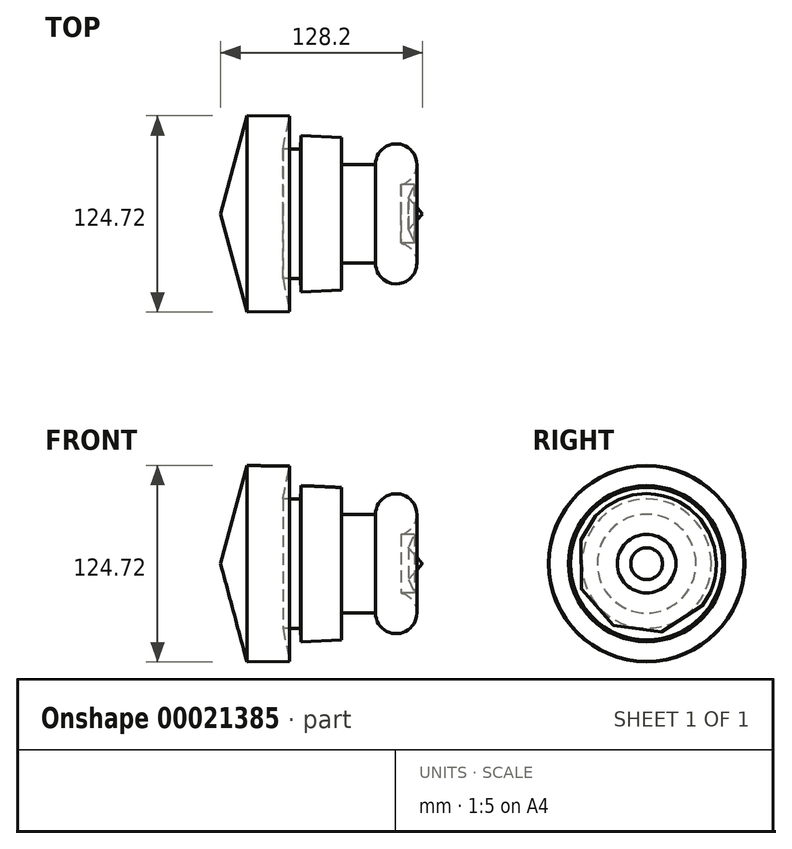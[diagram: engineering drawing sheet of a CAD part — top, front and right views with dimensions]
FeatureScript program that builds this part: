
annotation { "Feature Type Name" : "Feature", "Feature Type Description" : "" }
export const myFeature = defineFeature(function(context is Context, id is Id, definition is map)
    precondition{}
    {
        {
            var Q0;
            Q0=qCreatedBy(makeId("Front.planeOp"),FACE);
            var sketch = newSketch(context, id + "F0", { "sketchPlane" : qUnion([Q0])});
            skLineSegment(sketch, "E0", {"start": v(-63.13, 0) * mm, "end": v(65.07, 0) * mm});
            skLineSegment(sketch, "E1", {"start": v(65.07, 0) * mm, "end": v(56.16, 10.07) * mm});
            skLineSegment(sketch, "E2", {"start": v(56.16, 10.07) * mm, "end": v(60.03, 18.6) * mm});
            skLineSegment(sketch, "E3", {"start": v(60.03, 18.6) * mm, "end": v(45.32, 18.6) * mm});
            skArc(sketch, "E4", {"start": v(45.32, 18.6) * mm, "mid": v(58.65, 39.45) * mm, "end": v(35.25, 31.37) * mm});
            skLineSegment(sketch, "E5", {"start": v(35.25, 31.37) * mm, "end": v(13.56, 31.34) * mm});
            skLineSegment(sketch, "E6", {"start": v(13.56, 31.34) * mm, "end": v(13.53, 48.41) * mm});
            skLineSegment(sketch, "E7", {"start": v(13.53, 48.41) * mm, "end": v(-12, 49.58) * mm});
            skLineSegment(sketch, "E8", {"start": v(-12, 49.58) * mm, "end": v(-12.4, 41.05) * mm});
            skLineSegment(sketch, "E9", {"start": v(-12.4, 41.05) * mm, "end": v(-23.63, 41.05) * mm});
            skLineSegment(sketch, "E10", {"start": v(-23.63, 41.05) * mm, "end": v(-19.37, 61.97) * mm});
            skLineSegment(sketch, "E11", {"start": v(-19.37, 61.97) * mm, "end": v(-46.48, 62.36) * mm});
            skLineSegment(sketch, "E12", {"start": v(-46.48, 62.36) * mm, "end": v(-63.13, 0) * mm});
            skSolve(sketch);
        }
        {
            var Q0;
            Q0 = qSketchRegion(id + "F0", true);
            var Q1;
            Q1=sQuery(id+"F0.wireOp",EDGE,"E0");
            revolve(context, id + "F1", {"entities" : qUnion([Q0]), "axis" : qUnion([Q1]), "revolveType" : RevolveType.FULL});
        }
    });
